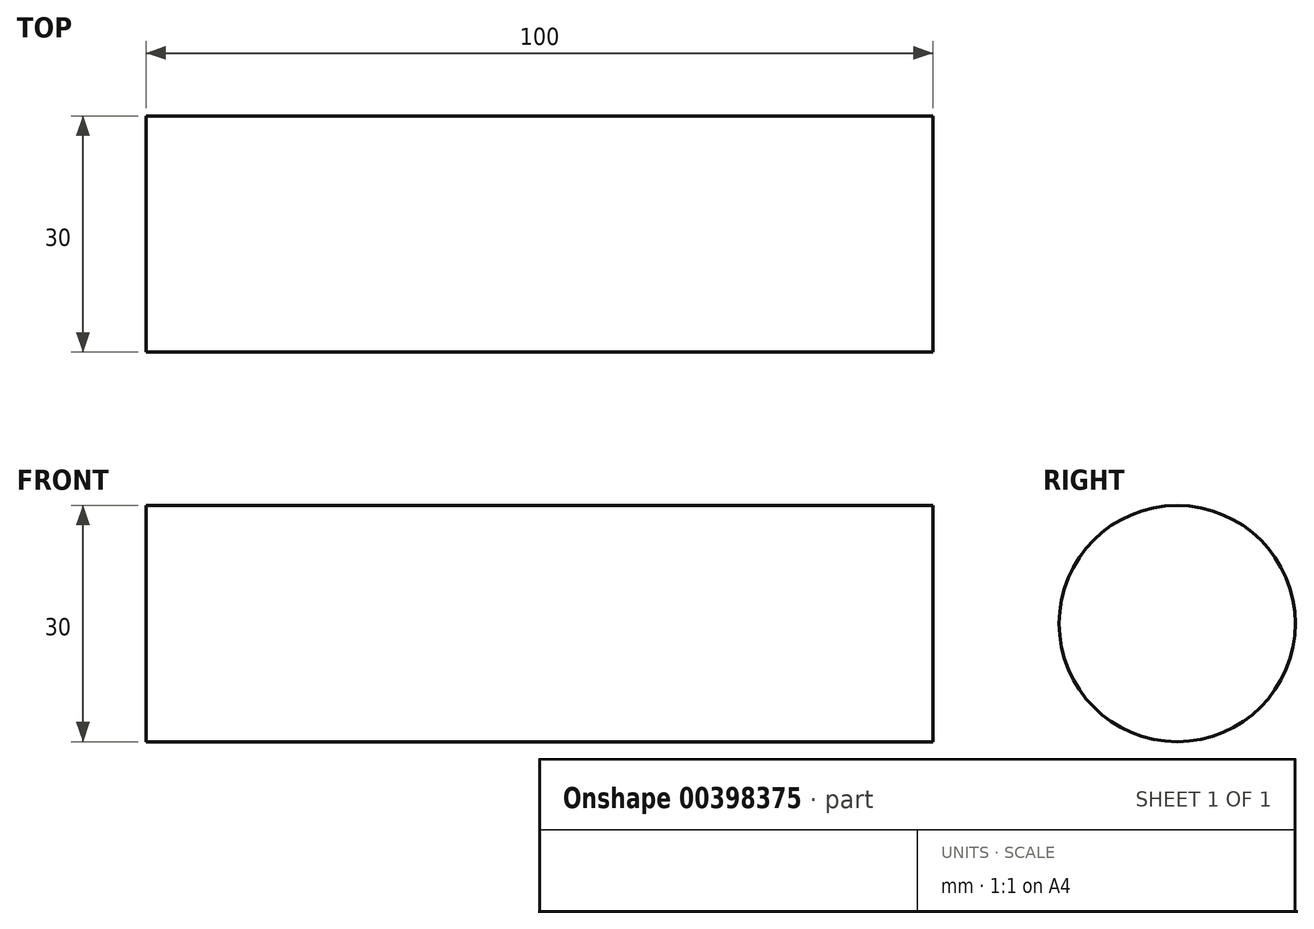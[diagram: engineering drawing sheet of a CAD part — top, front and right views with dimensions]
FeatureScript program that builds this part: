
annotation { "Feature Type Name" : "Feature", "Feature Type Description" : "" }
export const myFeature = defineFeature(function(context is Context, id is Id, definition is map)
    precondition{}
    {
        {
            var Q0;
            Q0=qCreatedBy(makeId("Front.planeOp"),FACE);
            var sketch = newSketch(context, id + "F0", { "sketchPlane" : qUnion([Q0])});
            skLineSegment(sketch, "E0.bottom", {"start": v(-50, 15) * mm, "end": v(50, 15) * mm});
            skLineSegment(sketch, "E0.top", {"start": v(-50, 0) * mm, "end": v(50, 0) * mm});
            skLineSegment(sketch, "E0.left", {"start": v(-50, 15) * mm, "end": v(-50, 0) * mm});
            skLineSegment(sketch, "E0.right", {"start": v(50, 15) * mm, "end": v(50, 0) * mm});
            skLineSegment(sketch, "E1", {"start": v(-85.48, 0) * mm, "end": v(76.56, 0) * mm, "construction": true});
            skSolve(sketch);
        }
        {
            var Q0;
            Q0=makeQuery(id+"F0.imprint","IMPRINT",FACE,{"disambiguationData":[TD([[makeQuery(id+"F0.imprint","IMPRINT",EDGE,{"derivedFrom":sQuery(id+"F0.wireOp",EDGE,"E0.bottom")}),-1.0]])]});
            var Q1;
            Q1=sQuery(id+"F0.wireOp",EDGE,"E1");
            var Q2;
            Q2=sQuery(id+"F0.wireOp",EDGE,"E0.bottom");
            var Q3;
            Q3=sQuery(id+"F0.wireOp",EDGE,"E0.left");
            var Q4;
            Q4=sQuery(id+"F0.wireOp",EDGE,"E0.right");
            var Q5;
            Q5=sQuery(id+"F0.wireOp",EDGE,"E1");
            revolve(context, id + "F1", {"entities" : qUnion([Q0]), "surfaceEntities" : qUnion([Q1, Q2, Q3, Q4]), "axis" : qUnion([Q5]), "revolveType" : RevolveType.FULL});
        }
    });
